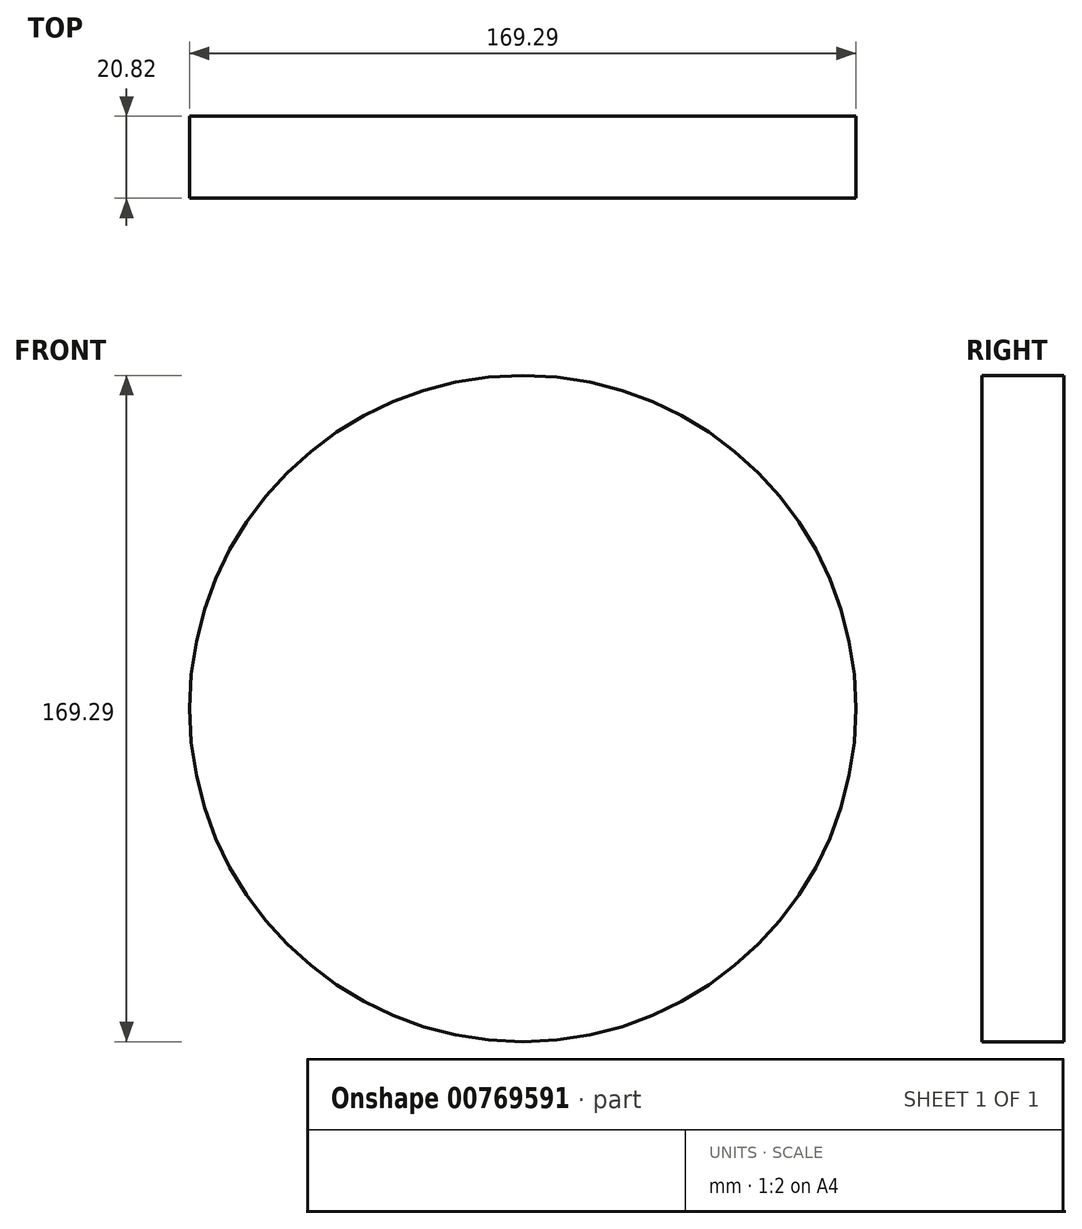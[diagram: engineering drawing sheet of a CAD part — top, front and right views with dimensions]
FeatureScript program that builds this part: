
annotation { "Feature Type Name" : "Feature", "Feature Type Description" : "" }
export const myFeature = defineFeature(function(context is Context, id is Id, definition is map)
    precondition{}
    {
        {
            var Q0;
            Q0=qCreatedBy(makeId("Front.planeOp"),FACE);
            var sketch = newSketch(context, id + "F0", { "sketchPlane" : qUnion([Q0])});
            skCircle(sketch, "E0", {"center": v(-43.9, 8.22) * mm, "radius": 84.64 * mm});
            skSolve(sketch);
        }
        {
            var Q0;
            Q0=makeQuery(id+"F0.imprint","IMPRINT",FACE,{"disambiguationData":[TD([[makeQuery(id+"F0.imprint","IMPRINT",EDGE,{"derivedFrom":sQuery(id+"F0.wireOp",EDGE,"E0")}),1.0]])]});
            extrude(context, id + "F1", {"entities" : qUnion([Q0]), "endBound" : BoundingType.SYMMETRIC, "depth" : 20.83 * mm, "offsetDistance" : 25.4 * mm});
        }
    });
